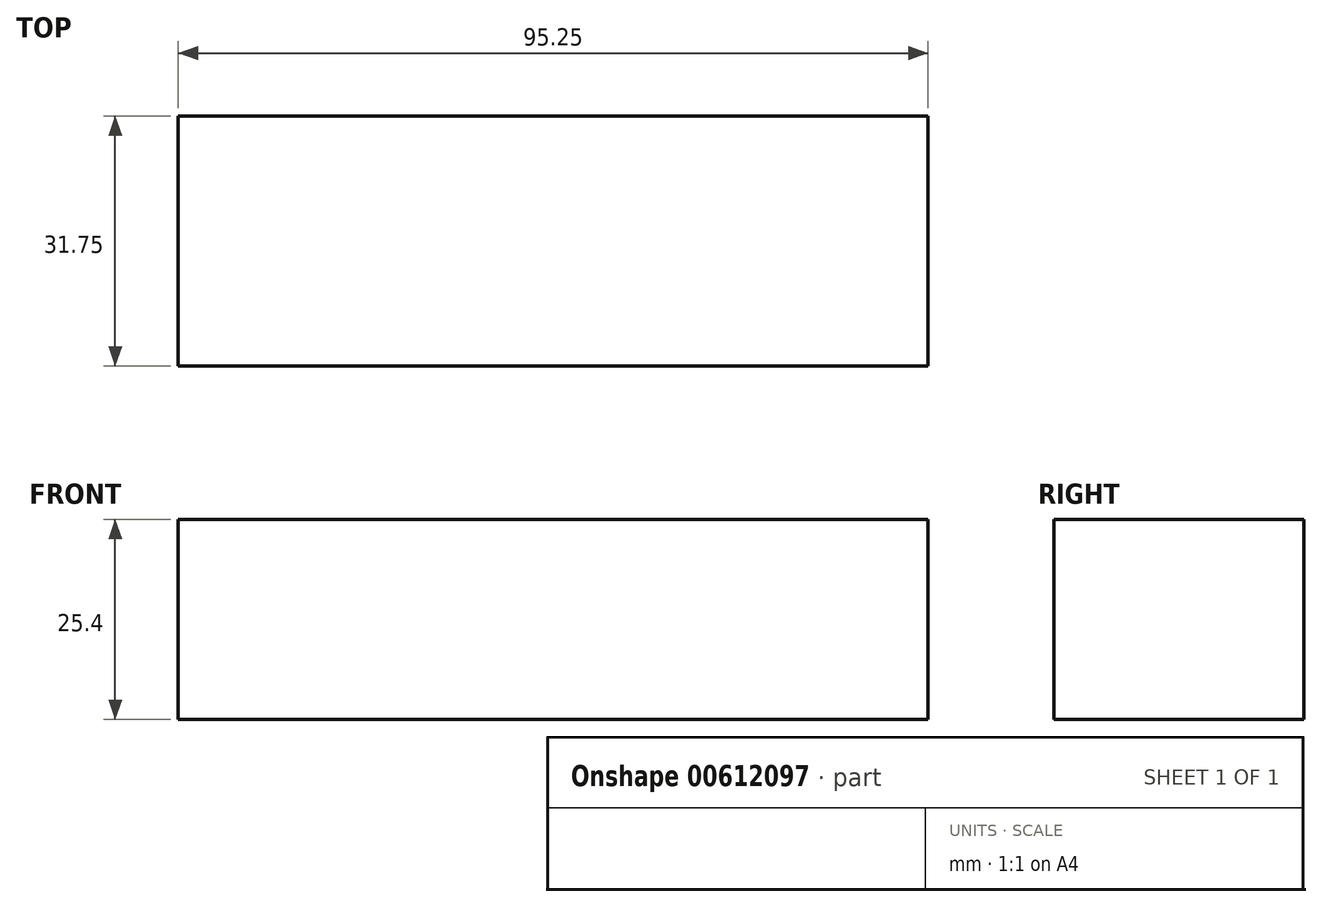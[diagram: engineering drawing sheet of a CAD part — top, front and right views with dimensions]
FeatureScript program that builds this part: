
annotation { "Feature Type Name" : "Feature", "Feature Type Description" : "" }
export const myFeature = defineFeature(function(context is Context, id is Id, definition is map)
    precondition{}
    {
        {
            var Q0;
            Q0=qCreatedBy(makeId("Top.planeOp"),FACE);
            var sketch = newSketch(context, id + "F0", { "sketchPlane" : qUnion([Q0])});
            skLineSegment(sketch, "E0.bottom", {"start": v(0, 31.75) * mm, "end": v(95.25, 31.75) * mm});
            skLineSegment(sketch, "E0.top", {"start": v(0, 0) * mm, "end": v(95.25, 0) * mm});
            skLineSegment(sketch, "E0.left", {"start": v(0, 31.75) * mm, "end": v(0, 0) * mm});
            skLineSegment(sketch, "E0.right", {"start": v(95.25, 31.75) * mm, "end": v(95.25, 0) * mm});
            skSolve(sketch);
        }
        {
            var Q0;
            Q0=makeQuery(id+"F0.imprint","IMPRINT",FACE,{"disambiguationData":[TD([[makeQuery(id+"F0.imprint","IMPRINT",EDGE,{"derivedFrom":sQuery(id+"F0.wireOp",EDGE,"E0.bottom")}),-1.0]])]});
            extrude(context, id + "F1", {"entities" : qUnion([Q0]), "depth" : 25.4 * mm, "offsetDistance" : 25.4 * mm});
        }
    });
